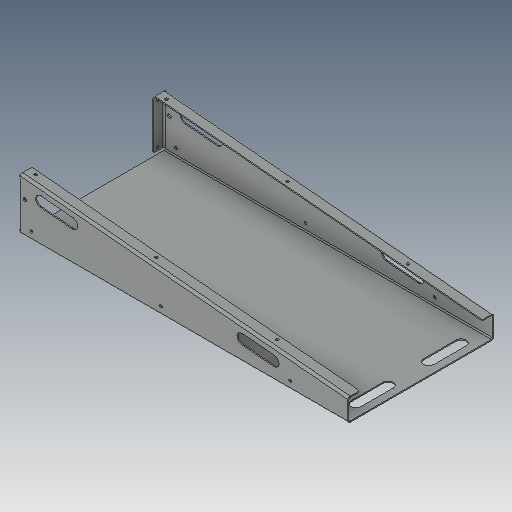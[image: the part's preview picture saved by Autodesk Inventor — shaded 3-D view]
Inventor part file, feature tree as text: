
AUTODESK INVENTOR PART (.ipt)
format: ipt  version: 2023.5 (Build 275446000, 446)  size: 203,776 bytes
history: native  units: in
note: dims shown in document units (in); Inventor stores cm internally (conversion verified against a paired STEP export)
features: fillet x1
ambient origin geometry x8: Origin, YZ Plane, XZ Plane, XY Plane, X Axis, Y Axis, Z Axis, Center Point
bodies: Solid1 (feature_tree)
feature tree (1):
  fillet  "Fillet3"  [1 undecoded]
note: 1 required parameter value undecoded (feature->parameter linkage not recoverable at this tier; creation-order binding heuristic only, values carry confidence <= 0.55)
